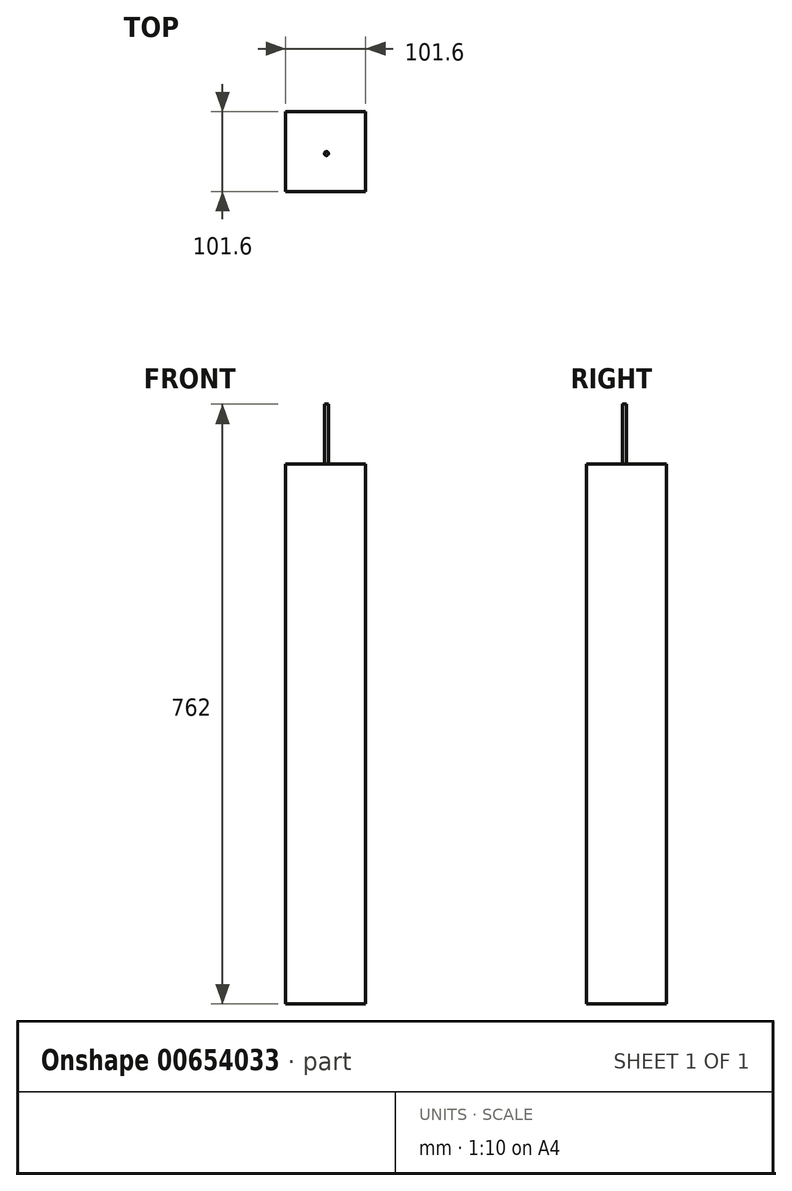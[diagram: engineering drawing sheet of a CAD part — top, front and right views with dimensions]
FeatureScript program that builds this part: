
annotation { "Feature Type Name" : "Feature", "Feature Type Description" : "" }
export const myFeature = defineFeature(function(context is Context, id is Id, definition is map)
    precondition{}
    {
        {
            var Q0;
            Q0=qCreatedBy(makeId("Top.planeOp"),FACE);
            var sketch = newSketch(context, id + "F0", { "sketchPlane" : qUnion([Q0])});
            skLineSegment(sketch, "E0.bottom", {"start": v(-45.76, 47.29) * mm, "end": v(55.84, 47.29) * mm});
            skLineSegment(sketch, "E0.top", {"start": v(-45.76, -54.31) * mm, "end": v(55.84, -54.31) * mm});
            skLineSegment(sketch, "E0.left", {"start": v(-45.76, 47.29) * mm, "end": v(-45.76, -54.31) * mm});
            skLineSegment(sketch, "E0.right", {"start": v(55.84, 47.29) * mm, "end": v(55.84, -54.31) * mm});
            skSolve(sketch);
        }
        {
            var Q0;
            Q0 = qSketchRegion(id + "F2", true);
            var Q1;
            Q1 = qSketchRegion(id + "F0", true);
            extrude(context, id + "F1", {"entities" : qUnion([Q0, Q1]), "depth" : 685.8 * mm, "offsetDistance" : 25.4 * mm});
        }
        {
            var Q0;
            Q0=makeQuery(id+"F1.opExtrude","CAP_FACE",FACE,{"disambiguationData":[OSD([sQuery(id+"F0.wireOp",EDGE,"E0.bottom"),sQuery(id+"F0.wireOp",EDGE,"E0.top"),sQuery(id+"F0.wireOp",EDGE,"E0.left"),sQuery(id+"F0.wireOp",EDGE,"E0.right")])],"isStart":false});
            var sketch = newSketch(context, id + "F2", { "sketchPlane" : qUnion([Q0])});
            skCircle(sketch, "E1", {"center": v(5.98, -5.94) * mm, "radius": 2.54 * mm});
            skSolve(sketch);
        }
        {
            var Q0;
            Q0=makeQuery(id+"F2.imprint","IMPRINT",FACE,{"disambiguationData":[TD([[makeQuery(id+"F2.imprint","IMPRINT",EDGE,{"derivedFrom":sQuery(id+"F2.wireOp",EDGE,"E1")}),1.0]])]});
            extrude(context, id + "F3", {"entities" : qUnion([Q0]), "operationType" : NewBodyOperationType.ADD, "depth" : 76.2 * mm, "offsetDistance" : 25.4 * mm});
        }
    });
